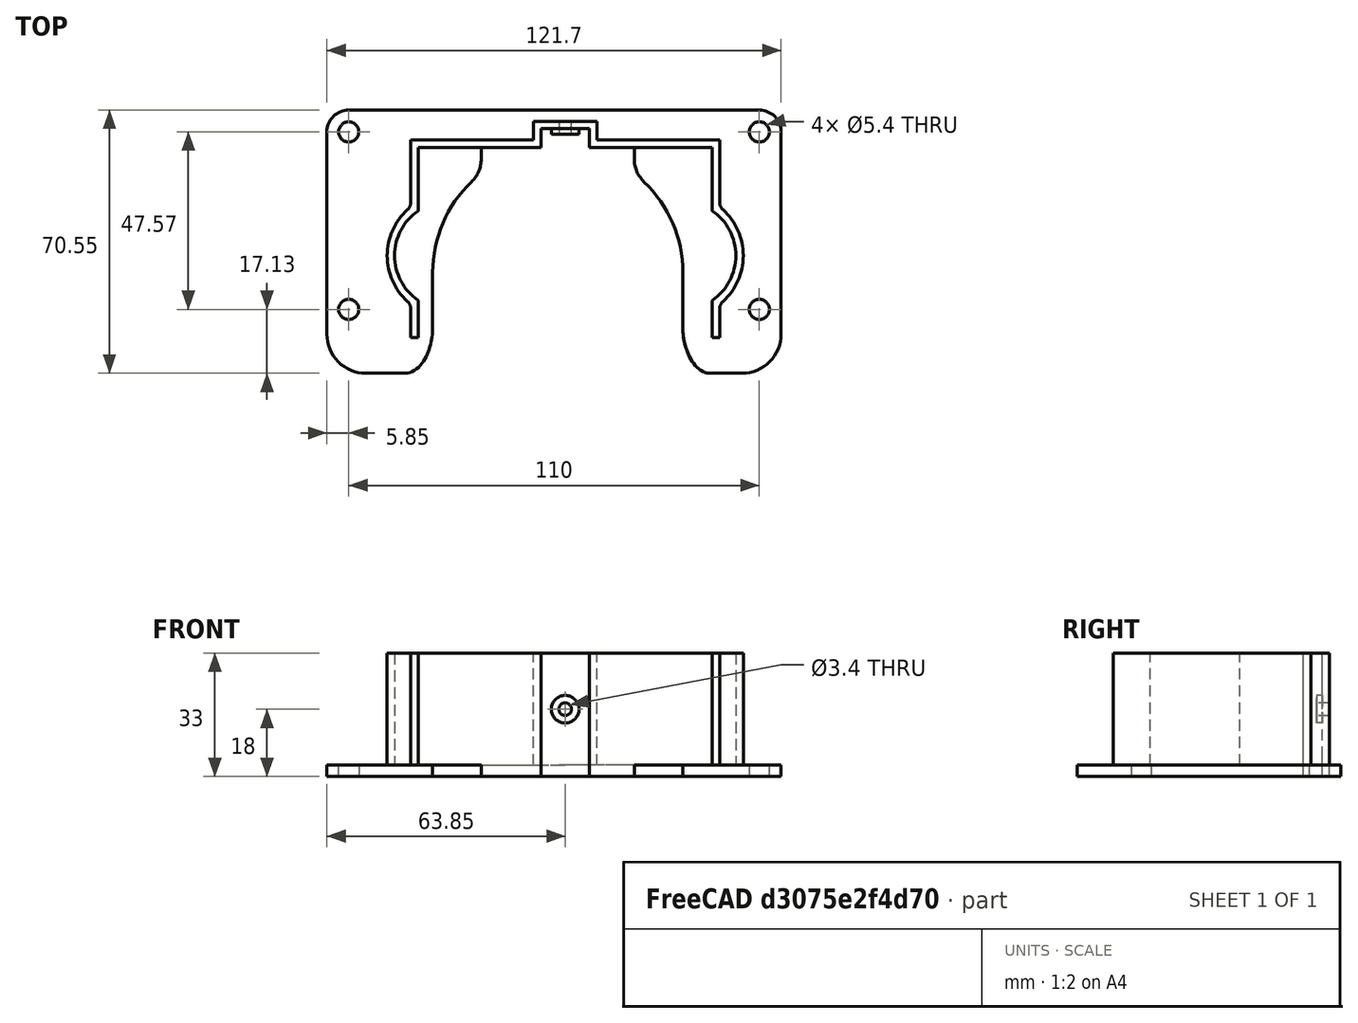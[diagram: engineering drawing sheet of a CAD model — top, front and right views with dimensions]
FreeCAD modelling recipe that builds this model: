
FCSTD DOCUMENT  (FreeCAD 0.20R29410 (Git))
Label: Направляющая датёра2
License: All rights reserved
LicenseURL: http://en.wikipedia.org/wiki/All_rights_reserved
objects: Sketcher::SketchObject×6, PartDesign::Pad×3, PartDesign::Pocket×3, PartDesign::Mirrored×3, Mesh::Feature×1, PartDesign::Body×1
note: 22 computed .brp shape members not serialized (recipe doc carries the construction recipe); baked Part::Feature solids carry a one-line shape summary decoded from their .brp

FEATURE [Mesh::Feature] _____________________________________7  label="Направляющая датёра7"
FEATURE [Sketcher::SketchObject] Sketch
  FullyConstrained = true
  MapMode = 5
  Support = -> [XY_Plane]
  sketch-geometry (8):
    g0: Circle CenterX=55 CenterY=30.15 CenterZ=0 NormalX=0 NormalY=0 NormalZ=1 AngleXU=0 Radius=2.7
    g1: Circle CenterX=55 CenterY=-17.42 CenterZ=0 NormalX=0 NormalY=0 NormalZ=1 AngleXU=0 Radius=2.7
    g2: ArcOfCircle CenterX=55 CenterY=30.15 CenterZ=0 NormalX=0 NormalY=0 NormalZ=1 AngleXU=0 Radius=5.85 StartAngle=6.28319 EndAngle=7.85398
    g3: ArcOfCircle CenterX=50.35 CenterY=-24.05 CenterZ=0 NormalX=0 NormalY=0 NormalZ=1 AngleXU=0 Radius=10.5 StartAngle=4.71239 EndAngle=6.28319
    g4: LineSegment StartX=55 StartY=36 StartZ=0 EndX=0 EndY=36 EndZ=0
    g5: LineSegment StartX=0 StartY=36 StartZ=0 EndX=0 EndY=-34.55 EndZ=0
    g6: LineSegment StartX=0 StartY=-34.55 StartZ=0 EndX=50.35 EndY=-34.55 EndZ=0
    g7: LineSegment StartX=60.85 StartY=-24.05 StartZ=0 EndX=60.85 EndY=30.15 EndZ=0
  constraints (25):
    c: Coincident(g2,g0)
    c: Coincident(g4,g2)
    c: PointOnObject(g4,g-2)
    c: Horizontal(g4)
    c: Coincident(g5,g4)
    c: PointOnObject(g5,g-2)
    c: Coincident(g6,g5)
    c: Coincident(g6,g3)
    c: Coincident(g7,g3)
    c: Coincident(g7,g2)
    c: Vertical(g7)
    c: Horizontal(g6)
    c: Diameter(g0) = 5.4
    c: Vertical(g1,g0)
    c: Equal(g1,g0)
    c: DistanceX(g0) = 55
    c: DistanceY(g0) = 30.15
    c: DistanceY(g1) = -17.42
    c: Diameter(g2) = 11.7
    c: Tangent(g2,g4)
    c: Tangent(g2,g7)
    c: Tangent(g3,g7)
    c: Tangent(g6,g3)
    c: Diameter(g3) = 21
    c: DistanceY(g5) = -34.55
FEATURE [Sketcher::SketchObject] Sketch001
  AttachmentOffset = pos=(1,0,0) rot=(0,0,1;0rad)
  FullyConstrained = true
  MapMode = 5
  Placement = pos=(1,0,0) rot=(0,0,1;0rad)
  Support = -> [XY_Plane]
  sketch-geometry (12):
    g0: LineSegment StartX=20.5 StartY=22.8809 StartZ=0 EndX=20.5 EndY=26 EndZ=0
    g1: LineSegment StartX=20.5 StartY=26 StartZ=0 EndX=0 EndY=26 EndZ=0
    g2: ArcOfCircle CenterX=29 CenterY=22.8809 CenterZ=0 NormalX=0 NormalY=0 NormalZ=1 AngleXU=0 Radius=8.5 StartAngle=3.14159 EndAngle=3.95024
    g3: ArcOfCircle CenterX=0 CenterY=-7.5 CenterZ=0 NormalX=0 NormalY=0 NormalZ=1 AngleXU=0 Radius=33.5 StartAngle=8.26042e-09 EndAngle=0.808649
    g4: LineSegment StartX=41 StartY=-34.55 StartZ=0 EndX=0 EndY=-34.55 EndZ=0
    g5: LineSegment StartX=0 StartY=-34.55 StartZ=0 EndX=0 EndY=26 EndZ=0
    g6: LineSegment StartX=33.5 StartY=-7.5 StartZ=0 EndX=33.5 EndY=-22 EndZ=0
    g7: ArcOfEllipse CenterX=41 CenterY=-22 CenterZ=0 NormalX=0 NormalY=0 NormalZ=1 MajorRadius=12.55 MinorRadius=7.5 AngleXU=1.5708 StartAngle=1.5708 EndAngle=3.14159
    g8: LineSegment StartX=41 StartY=-9.45 StartZ=0 EndX=41 EndY=-34.55 EndZ=0
    g9: LineSegment StartX=33.5 StartY=-22 StartZ=0 EndX=48.5 EndY=-22 EndZ=0
    g10: GeomPoint X=41 Y=-11.9376 Z=0
    g11: GeomPoint X=41 Y=-32.0624 Z=0
  constraints (30):
    c: Vertical(g0)
    c: Coincident(g1,g0)
    c: PointOnObject(g1,g-2)
    c: Horizontal(g1)
    c: Coincident(g2,g0)
    c: PointOnObject(g3,g-2)
    c: Coincident(g3,g2)
    c: PointOnObject(g4,g-2)
    c: Horizontal(g4)
    c: Coincident(g5,g4)
    c: Coincident(g5,g1)
    c: DistanceY(g4) = -34.55
    c: Coincident(g6,g3)
    c: Vertical(g6)
    c: Diameter(g3) = 67
    c: DistanceY(g1) = 26
    c: DistanceX(g0) = 20.5
    c: PointOnObject(g1,g3)
    c: Tangent(g3,g2)
    c: Tangent(g2,g0)
    c: Diameter(g2) = 17
    c: Tangent(g6,g3)
    c: InternalAlignment(g8-g11 -> g7) x4
    c: Coincident(g7,g4)
    c: Coincident(g7,g6)
    c: Vertical(g8)
    c: Tangent(g7,g6)
    c: Tangent(g7,g4)
    c: DistanceY(g6) = -22
    c: DistanceX(g4) = 41
FEATURE [Sketcher::SketchObject] Sketch002
  AttachmentOffset = pos=(3,-3,3) rot=(0,0,1;0rad)
  FullyConstrained = true
  MapMode = 5
  Placement = pos=(3,-3,3) rot=(0,0,1;0rad)
  Support = -> [XY_Plane]
  expr: Constraints[56] = Sketch001.Constraints[11]
  expr: Constraints[59] = Sketch001.Constraints[14]
  expr: Constraints[61] = Sketch001.Constraints[16]
  expr: Constraints[65] = Sketch001.Constraints[20]
  expr: Constraints[76] = Sketch001.Constraints[31]
  expr: Constraints[77] = Sketch001.Constraints[32]
  sketch-geometry (32):
    g0: LineSegment StartX=39.4162 StartY=-22 StartZ=0 EndX=41.4162 EndY=-22 EndZ=0
    g1: LineSegment StartX=39.4162 StartY=-22 StartZ=0 EndX=39.4162 EndY=-12 EndZ=0
    g2: LineSegment StartX=39.4162 StartY=12 StartZ=0 EndX=39.4162 EndY=29 EndZ=0
    g3: LineSegment StartX=39.4162 StartY=29 StartZ=0 EndX=6.5 EndY=29 EndZ=0
    g4: LineSegment StartX=6.5 StartY=29 StartZ=0 EndX=6.5 EndY=34 EndZ=0
    g5: LineSegment StartX=6.5 StartY=34 StartZ=0 EndX=0 EndY=34 EndZ=0
    g6: LineSegment StartX=41.4162 StartY=-22 StartZ=0 EndX=41.4162 EndY=-14.1617 EndZ=0
    g7: LineSegment StartX=41.4162 StartY=14.1617 StartZ=0 EndX=41.4162 EndY=31 EndZ=0
    g8: LineSegment StartX=41.4162 StartY=31 StartZ=0 EndX=8.5 EndY=31 EndZ=0
    g9: LineSegment StartX=8.5 StartY=31 StartZ=0 EndX=8.5 EndY=36 EndZ=0
    g10: LineSegment StartX=8.5 StartY=36 StartZ=0 EndX=0 EndY=36 EndZ=0
    g11: ArcOfCircle CenterX=31.1 CenterY=6e-16 CenterZ=0 NormalX=0 NormalY=0 NormalZ=1 AngleXU=0 Radius=14.6 StartAngle=5.31842 EndAngle=7.24796
    g12: ArcOfCircle CenterX=31.1 CenterY=6e-16 CenterZ=0 NormalX=0 NormalY=0 NormalZ=1 AngleXU=0 Radius=16.6 StartAngle=5.44796 EndAngle=7.11841
    g13: ArcOfCircle CenterX=43.9162 CenterY=14.1617 CenterZ=0 NormalX=0 NormalY=0 NormalZ=1 AngleXU=0 Radius=2.5 StartAngle=3.14159 EndAngle=3.97682
    g14: ArcOfCircle CenterX=43.9162 CenterY=-14.1617 CenterZ=0 NormalX=0 NormalY=0 NormalZ=1 AngleXU=0 Radius=2.5 StartAngle=2.30636 EndAngle=3.14159
    g15: LineSegment StartX=39.4162 StartY=29 StartZ=0 EndX=41.4162 EndY=29 EndZ=0
    g16: LineSegment StartX=8.5 StartY=31 StartZ=0 EndX=8.5 EndY=29 EndZ=0
    g17: LineSegment StartX=0 StartY=36 StartZ=0 EndX=0 EndY=34 EndZ=0
    g18: LineSegment StartX=20.5 StartY=25.8809 StartZ=0 EndX=20.5 EndY=29 EndZ=0
    g19: LineSegment StartX=20.5 StartY=29 StartZ=0 EndX=0 EndY=29 EndZ=0
    g20: ArcOfCircle CenterX=29 CenterY=25.8809 CenterZ=0 NormalX=0 NormalY=0 NormalZ=1 AngleXU=0 Radius=8.5 StartAngle=3.14159 EndAngle=3.95025
    g21: ArcOfCircle CenterX=0 CenterY=-4.5 CenterZ=0 NormalX=0 NormalY=0 NormalZ=1 AngleXU=0 Radius=33.5 StartAngle=6.28318 EndAngle=7.09183
    g22: LineSegment StartX=41 StartY=-34.55 StartZ=0 EndX=0 EndY=-34.55 EndZ=0
    g23: LineSegment StartX=0 StartY=-34.55 StartZ=0 EndX=0 EndY=29 EndZ=0
    g24: LineSegment StartX=33.5 StartY=-4.50003 StartZ=0 EndX=33.5 EndY=-22 EndZ=0
    g25: ArcOfEllipse CenterX=41 CenterY=-22 CenterZ=0 NormalX=0 NormalY=0 NormalZ=1 MajorRadius=12.55 MinorRadius=7.5 AngleXU=1.5708 StartAngle=1.5708 EndAngle=3.14159
    g26: LineSegment StartX=41 StartY=-9.45 StartZ=0 EndX=41 EndY=-34.55 EndZ=0
    g27: LineSegment StartX=33.5 StartY=-22 StartZ=0 EndX=48.5 EndY=-22 EndZ=0
    g28: GeomPoint X=41 Y=-11.9376 Z=0
    g29: GeomPoint X=41 Y=-32.0624 Z=0
    g30: LineSegment StartX=8.5 StartY=31 StartZ=0 EndX=6.5 EndY=31 EndZ=0
    g31: GeomPoint X=45.7 Y=0 Z=0
  constraints (91):
    c: Horizontal(g0)
    c: Coincident(g1,g0)
    c: Vertical(g1)
    c: Vertical(g2)
    c: Coincident(g3,g2)
    c: Horizontal(g3)
    c: Coincident(g4,g3)
    c: Vertical(g4)
    c: Coincident(g5,g4)
    c: Horizontal(g5)
    c: Coincident(g6,g0)
    c: Vertical(g6)
    c: Vertical(g7)
    c: Coincident(g8,g7)
    c: Horizontal(g8)
    c: Coincident(g9,g8)
    c: Vertical(g9)
    c: Coincident(g10,g9)
    c: PointOnObject(g10,g-2)
    c: Horizontal(g10)
    c: Coincident(g11,g1)
    c: Coincident(g11,g2)
    c: DistanceY(g1) = -12
    c: Diameter(g11) = 29.2
    c: Coincident(g12,g11)
    c: Diameter(g12) = 33.2
    c: Coincident(g13,g12)
    c: Coincident(g13,g7)
    c: Coincident(g14,g6)
    c: Coincident(g14,g12)
    c: Diameter(g14) = 5
    c: Distance(g0) = 2
    c: Coincident(g15,g2)
    c: PointOnObject(g15,g7)
    c: Horizontal(g15)
    c: Equal(g0,g15)
    c: Coincident(g16,g8)
    c: PointOnObject(g16,g3)
    c: Vertical(g16)
    c: Equal(g16,g15)
    c: Equal(g14,g13)
    c: Distance(g4) = 5
    c: Coincident(g17,g10)
    c: Coincident(g17,g5)
    c: Vertical(g17)
    c: Vertical(g18)
    c: Coincident(g19,g18)
    c: PointOnObject(g19,g-2)
    c: Horizontal(g19)
    c: Coincident(g20,g18)
    c: PointOnObject(g21,g-2)
    c: Coincident(g21,g20)
    c: PointOnObject(g22,g-2)
    c: Horizontal(g22)
    c: Coincident(g23,g22)
    c: Coincident(g23,g19)
    c: DistanceY(g22) = -34.55
    c: Coincident(g24,g21)
    c: Vertical(g24)
    c: Diameter(g21) = 67
    c: DistanceY(g19) = 29
    c: DistanceX(g18) = 20.5
    c: PointOnObject(g19,g21)
    c: Tangent(g21,g20)
    c: Tangent(g20,g18)
    c: Diameter(g20) = 17
    c: Tangent(g24,g21)
    c: InternalAlignment(g26-g29 -> g25) x4
    c: Coincident(g25,g22)
    c: Coincident(g25,g24)
    c: Vertical(g26)
    c: Tangent(g25,g24)
    c: Tangent(g25,g22)
    c: DistanceY(g24) = -22
    c: DistanceX(g22) = 41
    c: PointOnObject(g3,g19)
    c: Coincident(g30,g8)
    c: PointOnObject(g30,g4)
    c: Horizontal(g30)
    c: Equal(g16,g30)
    c: Distance(g5) = 6.5
    c: Equal(g0,g17)
    c: Tangent(g13,g7)
    c: Tangent(g12,g13)
    c: Tangent(g12,g14)
    c: Tangent(g14,g6)
    c: Distance(g1) = 10
    c: Symmetric(g1,g2,g-1)
    c: PointOnObject(g31,g11)
    c: PointOnObject(g31,g-1)
    c: DistanceX(g31) = 45.7
FEATURE [PartDesign::Pad] Pad
  Direction = (0,0,1)
  Length = 3
  Length2 = 100
  Profile = -> Sketch
  Type = 0
FEATURE [PartDesign::Pocket] Pocket
  BaseFeature = -> Pad
  Direction = (0,0,-1)
  Length = 5
  Length2 = 100
  Profile = -> Sketch001
  Reversed = true
  Type = 0
FEATURE [PartDesign::Pad] Pad001
  BaseFeature = -> Pocket
  Direction = (0,0,1)
  Length = 30
  Length2 = 100
  Profile = -> Sketch002
  Type = 0
FEATURE [Sketcher::SketchObject] Sketch004
  AttachmentOffset = pos=(3,0,0) rot=(0,0,1;0rad)
  FullyConstrained = true
  MapMode = 5
  Placement = pos=(3,0,0) rot=(0,0,1;0rad)
  Support = -> [XY_Plane]
  sketch-geometry (4):
    g0: LineSegment StartX=0 StartY=26 StartZ=0 EndX=6.5 EndY=26 EndZ=0
    g1: LineSegment StartX=6.5 StartY=26 StartZ=0 EndX=6.5 EndY=31 EndZ=0
    g2: LineSegment StartX=6.5 StartY=31 StartZ=0 EndX=0 EndY=31 EndZ=0
    g3: LineSegment StartX=0 StartY=31 StartZ=0 EndX=0 EndY=26 EndZ=0
  constraints (12):
    c: Coincident(g0,g1)
    c: Coincident(g1,g2)
    c: Coincident(g2,g3)
    c: Coincident(g3,g0)
    c: Horizontal(g0)
    c: Horizontal(g2)
    c: Vertical(g1)
    c: Vertical(g3)
    c: PointOnObject(g0,g-2)
    c: DistanceY(g0) = 26
    c: Distance(g3) = 5
    c: Distance(g0) = 6.5
FEATURE [Sketcher::SketchObject] Sketch005
  AttachmentOffset = pos=(3,0,-29.5) rot=(0,0,1;0rad)
  FullyConstrained = true
  MapMode = 5
  Placement = pos=(3,29.5,6.6e-15) rot=(1,0,0;1.5708rad)
  Support = -> [XZ_Plane]
  sketch-geometry (1):
    g0: Circle CenterX=0 CenterY=18 CenterZ=0 NormalX=0 NormalY=0 NormalZ=1 AngleXU=0 Radius=3.7
  constraints (3):
    c: Diameter(g0) = 7.4
    c: DistanceY(g0) = 18
    c: PointOnObject(g0,g-2)
FEATURE [Sketcher::SketchObject] Sketch006
  AttachmentOffset = pos=(3,0,0) rot=(0,0,1;0rad)
  FullyConstrained = true
  MapMode = 5
  Placement = pos=(3,0,0) rot=(1,0,0;1.5708rad)
  Support = -> [XZ_Plane]
  expr: Constraints[1] = Sketch005.Constraints[1]
  sketch-geometry (1):
    g0: Circle CenterX=0 CenterY=18 CenterZ=0 NormalX=0 NormalY=0 NormalZ=1 AngleXU=0 Radius=1.7
  constraints (3):
    c: Diameter(g0) = 3.4
    c: DistanceY(g0) = 18
    c: PointOnObject(g0,g-2)
FEATURE [PartDesign::Pocket] Pocket001
  BaseFeature = -> Pad001
  Direction = (0,0,-1)
  Length = 5
  Length2 = 100
  Profile = -> Sketch004
  Reversed = true
  Type = 0
FEATURE [PartDesign::Mirrored] Mirrored
  BaseFeature = -> Pocket001
  MirrorPlane = -> Sketch [V_Axis]
  Originals = -> [Pad]
FEATURE [PartDesign::Mirrored] Mirrored001
  BaseFeature = -> Mirrored
  MirrorPlane = -> Sketch001 [V_Axis]
  Originals = -> [Pocket]
FEATURE [PartDesign::Mirrored] Mirrored002
  BaseFeature = -> Mirrored001
  MirrorPlane = -> Sketch002 [V_Axis]
  Originals = -> [Pad001,Pocket001]
FEATURE [PartDesign::Pad] Pad002
  BaseFeature = -> Mirrored002
  Direction = (0,-1,-2e-16)
  Length = 10
  Length2 = 100
  Profile = -> Sketch005
  Reversed = true
  Type = 1
FEATURE [PartDesign::Pocket] Pocket002
  BaseFeature = -> Pad002
  Direction = (0,1,2e-16)
  Length = 5
  Length2 = 100
  Profile = -> Sketch006
  Type = 1
FEATURE [PartDesign::Body] Body
  Group = -> [Sketch,Sketch001,Sketch002,Pad,Pocket,Pad001,Sketch004,Sketch005,Sketch006,Pocket001,Mirrored,Mirrored001,Mirrored002,Pad002,Pocket002]
  Origin = -> Origin
  Tip = -> Pocket002
